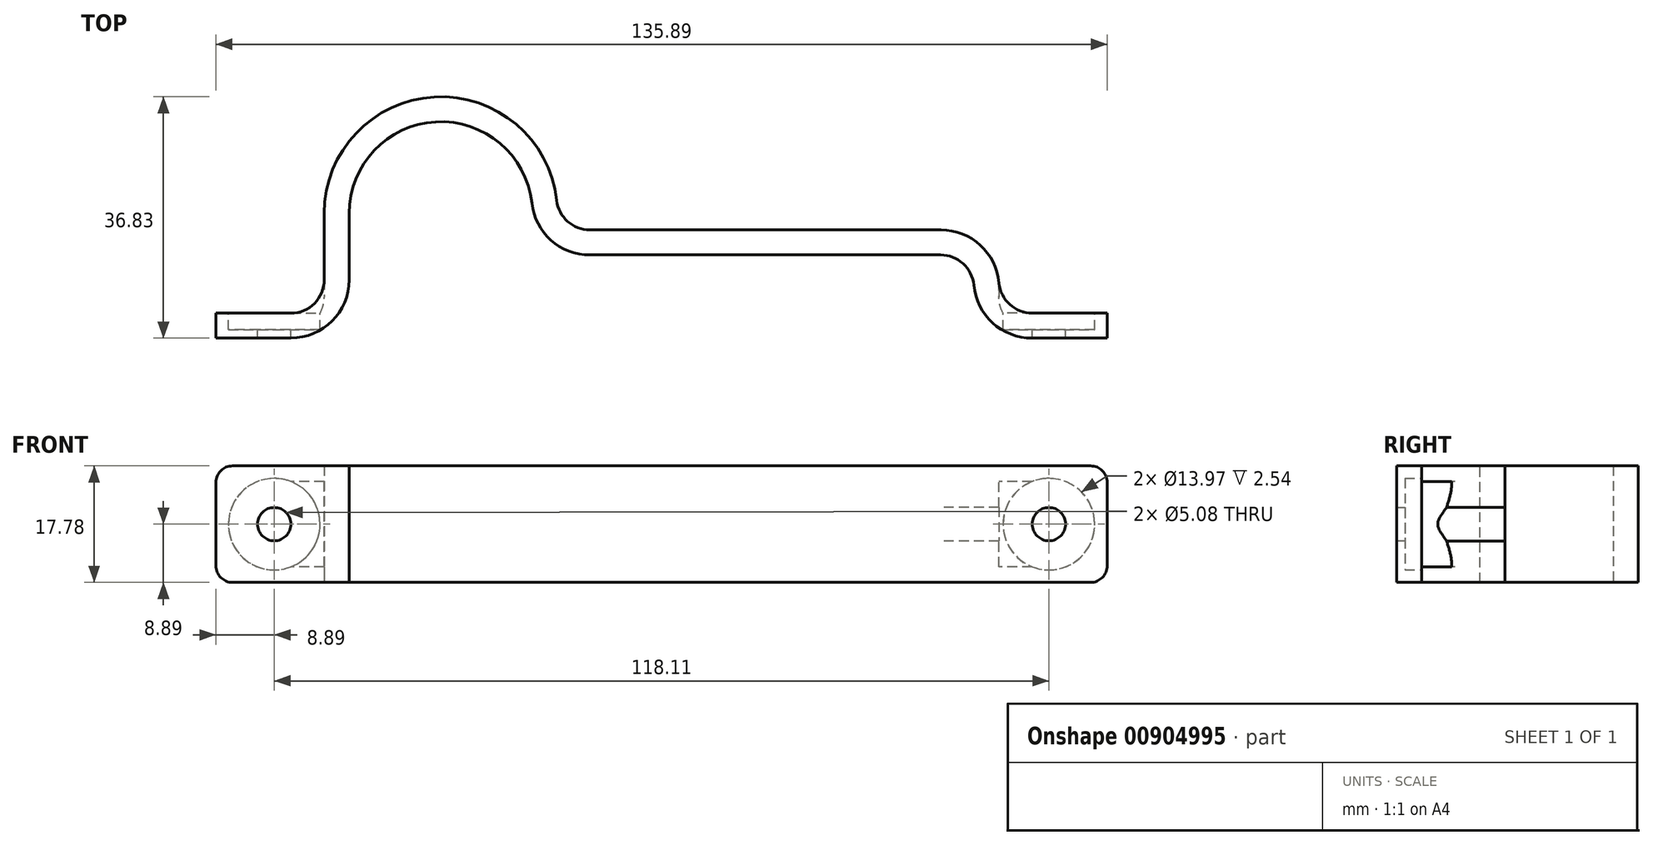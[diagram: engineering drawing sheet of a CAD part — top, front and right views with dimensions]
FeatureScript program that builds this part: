
annotation { "Feature Type Name" : "Feature", "Feature Type Description" : "" }
export const myFeature = defineFeature(function(context is Context, id is Id, definition is map)
    precondition{}
    {
        {
            var Q0;
            Q0=qCreatedBy(makeId("Top.planeOp"),FACE);
            var sketch = newSketch(context, id + "F0", { "sketchPlane" : qUnion([Q0])});
            skLineSegment(sketch, "E0", {"start": v(0, 0) * mm, "end": v(20.32, 0) * mm});
            skLineSegment(sketch, "E1", {"start": v(20.32, 0) * mm, "end": v(20.32, 19.05) * mm});
            skArc(sketch, "E2", {"start": v(48.26, 19.05) * mm, "mid": v(34.3, 33.02) * mm, "end": v(20.32, 19.05) * mm});
            skPoint(sketch, "E2.second.point", {"position": v(48.26, 19.05) * mm});
            skPoint(sketch, "E2.third.point", {"position": v(32.36, 5.21) * mm});
            skLineSegment(sketch, "E3", {"start": v(48.26, 19.05) * mm, "end": v(48.26, 12.7) * mm});
            skLineSegment(sketch, "E4", {"start": v(48.26, 12.7) * mm, "end": v(115.57, 12.7) * mm});
            skLineSegment(sketch, "E5", {"start": v(115.57, 12.7) * mm, "end": v(115.57, 0) * mm});
            skLineSegment(sketch, "E6", {"start": v(115.57, 0) * mm, "end": v(135.9, 0) * mm});
            skLineSegment(sketch, "E7.0", {"start": v(119.38, 3.81) * mm, "end": v(135.9, 3.81) * mm});
            skLineSegment(sketch, "E7.1", {"start": v(119.38, 16.51) * mm, "end": v(119.38, 3.81) * mm});
            skLineSegment(sketch, "E7.2", {"start": v(52.07, 16.5) * mm, "end": v(119.38, 16.51) * mm});
            skLineSegment(sketch, "E7.3", {"start": v(0, 3.81) * mm, "end": v(16.51, 3.81) * mm});
            skLineSegment(sketch, "E7.4", {"start": v(16.51, 3.81) * mm, "end": v(16.51, 19.05) * mm});
            skArc(sketch, "E7.5", {"start": v(52.07, 19.05) * mm, "mid": v(34.3, 36.83) * mm, "end": v(16.51, 19.05) * mm});
            skLineSegment(sketch, "E7.6", {"start": v(52.07, 19.05) * mm, "end": v(52.07, 16.5) * mm});
            skLineSegment(sketch, "E8", {"start": v(0, 0) * mm, "end": v(0, 3.81) * mm});
            skLineSegment(sketch, "E9", {"start": v(135.9, 3.81) * mm, "end": v(135.9, 0) * mm});
            skSolve(sketch);
        }
        {
            var Q0;
            Q0=makeQuery(id+"F0.imprint","IMPRINT",FACE,{"disambiguationData":[TD([[makeQuery(id+"F0.imprint","IMPRINT",EDGE,{"derivedFrom":sQuery(id+"F0.wireOp",EDGE,"E0")}),1.0]])]});
            extrude(context, id + "F1", {"entities" : qUnion([Q0]), "depth" : 17.78 * mm, "offsetDistance" : 25.4 * mm});
        }
        {
            var Q0;
            Q0=makeQuery(id+"F1.opExtrude","SWEPT_FACE",FACE,{"disambiguationData":[OSD([sQuery(id+"F0.wireOp",EDGE,"E7.3")])]});
            var sketch = newSketch(context, id + "F2", { "sketchPlane" : qUnion([Q0])});
            skCircle(sketch, "E10", {"center": v(-8.9, 8.9) * mm, "radius": 6.99 * mm});
            skCircle(sketch, "E11", {"center": v(-127, 8.89) * mm, "radius": 6.99 * mm});
            skSolve(sketch);
        }
        {
            var Q0;
            Q0 = qSketchRegion(id + "F2", true);
            extrude(context, id + "F3", {"entities" : qUnion([Q0]), "operationType" : NewBodyOperationType.REMOVE, "oppositeDirection" : true, "depth" : 2.54 * mm, "offsetDistance" : 25.4 * mm});
        }
        {
            var Q0;
            Q0=makeQuery(id+"F3.boolean.opBoolean","COPY",FACE,{"derivedFrom":makeQuery(id+"F3.opExtrude","CAP_FACE",FACE,{"disambiguationData":[OSD([sQuery(id+"F2.wireOp",EDGE,"E10")])],"isStart":false})});
            var sketch = newSketch(context, id + "F4", { "sketchPlane" : qUnion([Q0])});
            skCircle(sketch, "E12", {"center": v(-8.9, 8.9) * mm, "radius": 2.54 * mm});
            skSolve(sketch);
        }
        {
            var Q0;
            Q0 = qSketchRegion(id + "F4", true);
            extrude(context, id + "F5", {"entities" : qUnion([Q0]), "operationType" : NewBodyOperationType.REMOVE, "oppositeDirection" : true, "depth" : 25.4 * mm, "offsetDistance" : 25.4 * mm});
        }
        {
            var Q0;
            Q0=makeQuery(id+"F3.boolean.opBoolean","COPY",FACE,{"derivedFrom":makeQuery(id+"F3.opExtrude","CAP_FACE",FACE,{"disambiguationData":[OSD([sQuery(id+"F2.wireOp",EDGE,"E11")])],"isStart":false})});
            var sketch = newSketch(context, id + "F6", { "sketchPlane" : qUnion([Q0])});
            skCircle(sketch, "E13", {"center": v(-127, 8.89) * mm, "radius": 2.54 * mm});
            skSolve(sketch);
        }
        {
            var Q0;
            Q0 = qSketchRegion(id + "F6", true);
            extrude(context, id + "F7", {"entities" : qUnion([Q0]), "operationType" : NewBodyOperationType.REMOVE, "oppositeDirection" : true, "depth" : 25.4 * mm, "offsetDistance" : 25.4 * mm});
        }
        {
            var Q0;
            Q0=makeQuery(id+"F1.opExtrude","SWEPT_EDGE",EDGE,{"disambiguationData":[OSD([sQuery(id+"F0.wireOp",EDGE,"E7.3"),sQuery(id+"F0.wireOp",EDGE,"E7.4")])]});
            var Q1;
            Q1=makeQuery(id+"F1.opExtrude","SWEPT_EDGE",EDGE,{"disambiguationData":[OSD([sQuery(id+"F0.wireOp",EDGE,"E7.2"),sQuery(id+"F0.wireOp",EDGE,"E7.6")])]});
            var Q2;
            Q2=makeQuery(id+"F1.opExtrude","SWEPT_EDGE",EDGE,{"disambiguationData":[OSD([sQuery(id+"F0.wireOp",EDGE,"E7.0"),sQuery(id+"F0.wireOp",EDGE,"E7.1")])]});
            var Q3;
            Q3=makeQuery(id+"F1.opExtrude","SWEPT_EDGE",EDGE,{"disambiguationData":[OSD([sQuery(id+"F0.wireOp",EDGE,"E4"),sQuery(id+"F0.wireOp",EDGE,"E5")])]});
            fillet(context, id + "F8", {"entities" : qUnion([Q0, Q1, Q2, Q3]), "radius" : 5.08 * mm, "tangentPropagation" : true, "allowEdgeOverflow" : false});
        }
        {
            var Q0;
            Q0=makeQuery(id+"F1.opExtrude","SWEPT_EDGE",EDGE,{"disambiguationData":[OSD([sQuery(id+"F0.wireOp",EDGE,"E3"),sQuery(id+"F0.wireOp",EDGE,"E4")])]});
            var Q1;
            Q1=makeQuery(id+"F1.opExtrude","SWEPT_EDGE",EDGE,{"disambiguationData":[OSD([sQuery(id+"F0.wireOp",EDGE,"E7.1"),sQuery(id+"F0.wireOp",EDGE,"E7.2")])]});
            var Q2;
            Q2=makeQuery(id+"F1.opExtrude","SWEPT_EDGE",EDGE,{"disambiguationData":[OSD([sQuery(id+"F0.wireOp",EDGE,"E5"),sQuery(id+"F0.wireOp",EDGE,"E6")])]});
            var Q3;
            Q3=makeQuery(id+"F1.opExtrude","SWEPT_EDGE",EDGE,{"disambiguationData":[OSD([sQuery(id+"F0.wireOp",EDGE,"E0"),sQuery(id+"F0.wireOp",EDGE,"E1")])]});
            fillet(context, id + "F9", {"entities" : qUnion([Q0, Q1, Q2, Q3]), "radius" : 8.9 * mm, "tangentPropagation" : true, "allowEdgeOverflow" : false});
        }
        {
            var Q0;
            Q0=makeQuery(id+"F1.opExtrude","CAP_EDGE",EDGE,{"disambiguationData":[OSD([sQuery(id+"F0.wireOp",EDGE,"E8")])],"isStart":false});
            var Q1;
            Q1=makeQuery(id+"F1.opExtrude","CAP_EDGE",EDGE,{"disambiguationData":[OSD([sQuery(id+"F0.wireOp",EDGE,"E9")])],"isStart":false});
            var Q2;
            Q2=makeQuery(id+"F1.opExtrude","CAP_EDGE",EDGE,{"disambiguationData":[OSD([sQuery(id+"F0.wireOp",EDGE,"E8")])],"isStart":true});
            var Q3;
            Q3=makeQuery(id+"F1.opExtrude","CAP_EDGE",EDGE,{"disambiguationData":[OSD([sQuery(id+"F0.wireOp",EDGE,"E9")])],"isStart":true});
            fillet(context, id + "F10", {"entities" : qUnion([Q0, Q1, Q2, Q3]), "radius" : 2.54 * mm, "tangentPropagation" : true, "allowEdgeOverflow" : false});
        }
    });
